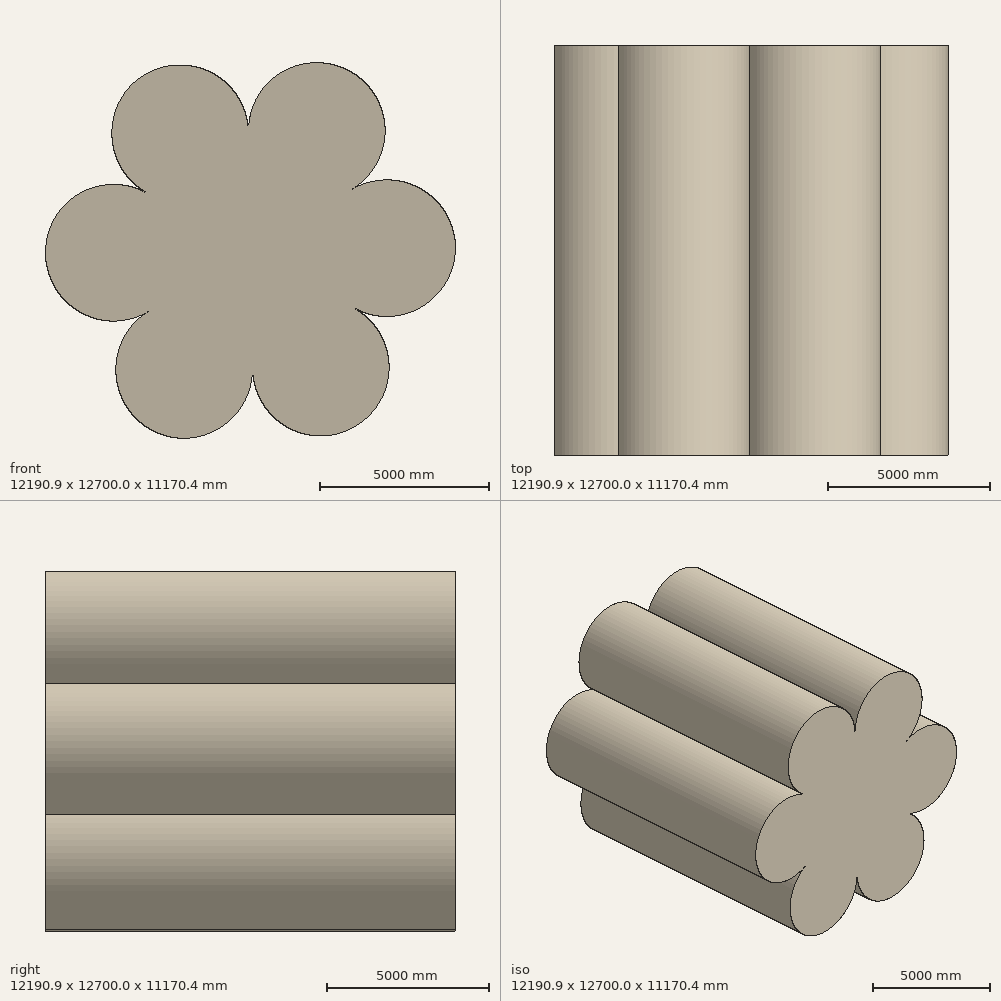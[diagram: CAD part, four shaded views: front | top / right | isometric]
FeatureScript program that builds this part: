
annotation { "Feature Type Name" : "Feature", "Feature Type Description" : "" }
export const myFeature = defineFeature(function(context is Context, id is Id, definition is map)
    precondition{}
    {
        {
            var Q0;
            Q0=qCreatedBy(makeId("Front.planeOp"),FACE);
            var sketch = newSketch(context, id + "F0", { "sketchPlane" : qUnion([Q0])});
            skCircle(sketch, "E0.cCircle", {"center": v(0, 0) * mm, "radius": 3519.53 * mm, "construction": true});
            skLineSegment(sketch, "E0.0", {"start": v(1972.51, 3553.2) * mm, "end": v(4063.43, 68.36) * mm, "construction": true});
            skLineSegment(sketch, "E0.1", {"start": v(4063.43, 68.36) * mm, "end": v(2090.91, -3484.85) * mm, "construction": true});
            skLineSegment(sketch, "E0.2", {"start": v(2090.91, -3484.85) * mm, "end": v(-1972.51, -3553.2) * mm, "construction": true});
            skLineSegment(sketch, "E0.3", {"start": v(-1972.51, -3553.2) * mm, "end": v(-4063.43, -68.36) * mm, "construction": true});
            skLineSegment(sketch, "E0.4", {"start": v(-4063.43, -68.36) * mm, "end": v(-2090.91, 3484.85) * mm, "construction": true});
            skLineSegment(sketch, "E0.5", {"start": v(-2090.91, 3484.85) * mm, "end": v(1972.51, 3553.2) * mm, "construction": true});
            skPoint(sketch, "E0.0.midPoint", {"position": v(3017.97, 1810.78) * mm});
            skCircle(sketch, "E1", {"center": v(-2090.91, 3484.85) * mm, "radius": 2032 * mm});
            skCircle(sketch, "E2", {"center": v(1972.51, 3553.2) * mm, "radius": 2032 * mm});
            skCircle(sketch, "E3", {"center": v(4063.43, 68.36) * mm, "radius": 2032 * mm});
            skCircle(sketch, "E4", {"center": v(2090.91, -3484.85) * mm, "radius": 2032 * mm});
            skCircle(sketch, "E5", {"center": v(-1972.51, -3553.2) * mm, "radius": 2032 * mm});
            skCircle(sketch, "E6", {"center": v(-4063.43, -68.36) * mm, "radius": 2032 * mm});
            skCircle(sketch, "E7", {"center": v(0, 0) * mm, "radius": 6096 * mm, "construction": true});
            skSolve(sketch);
        }
        {
            var Q0;
            Q0 = qSketchRegion(id + "F0", true);
            extrude(context, id + "F1", {"entities" : qUnion([Q0]), "depth" : 12700 * mm, "offsetDistance" : 25.4 * mm});
        }
    });
